# Revit family: QF_Friginox_MX 1 LA TS7-AC
name_source: partatom
category: Specialty Equipment
units: mm (PartAtom-declared; Revit-internal decimal feet)

## family parameters
Always vertical = Yes
Cut with Voids When Loaded = No
Part Type = Normal
Room Calculation Point = No
Round Connector Dimension = Use Diameter
Shared = No
Work Plane-Based = No

## types (2) — shared parameters
Accessory = No
CE Approved = Yes
Chilled Water Return Size = 0 mm
Chilled Water Supply Flow = 0.0 L/s
Chilled Water Supply Size = 0 mm
Condensate Return Connection Height = 105 mm  [stored 0.344488 ft]
Condensate Return Size = 32 mm
Conn Plug = Only cable
Cycle = 50 Hz
D15 = 15 mm  [stored 0.0492126 ft]
Depth Actual = 1091 mm
Description = Blast Chiller, Roll-in 1 trolley GN1/1, 80kg, 110min
Direct Waste Size = 20 mm
Direct Waste_Note = Direct Waste
Door_Depth = 131 mm  [stored 0.42979 ft]
Door_W = 650 mm  [stored 2.13255 ft]
Elec Connection Height = 2030 mm  [stored 6.6601 ft]
Electric power = 5700 W
FL Amps = 0 A
Foodservice Equipment Identifier = Yes
Groupe frigorifique = Logé
Height Actual = 2420 mm  [stored 7.93963 ft]
Identify Quantity as Lot = No
Item Number = FX39272636
Keynote = 0
Length Actual = 1080 mm  [stored 3.54331 ft]
Main switch integrated = No
Manufacturer = FRIGINOX
Mat_Case = QF_Stainless-Brushed
Mat_Clearance = QF_Clearance
Mat_Legs = QF_Stainless-Brushed
Model = MX 1 LA TS7
Number of Poles = 3
Phase = 3
Potential Equalisation = Yes
Refrigerant Compressor Remote = No
Refrigerant Volume = 0.0 L/s
Refrigeration Defrost Drain = Yes
Refrigeration Liquid Line Size = 10 mm
Refrigeration Suction Line Size = 28 mm
URL Cutsheet = FTEC_MX1LATS7_MX1LSTS7_MX1LSXTS7_SXP1LcATS7_SXP1LcSTS7_FR_0922.pdf
URL Manufacturer = http://www.friginox.com
Volt Free Conn = No
Volts = 400 V
Weight = 260.00 kg
zero-valued in all types: Chilled Water Return Connection Height, Chilled Water Supply Connection Height, Cost, Default Elevation, Direct Waste Connection Height, Refrigerant Mass

## per-type parameters (varying)
| type | LH | RH |
| MX 1 LA TS7_RH | No | Yes |
| MX 1 LA TS7_LH | Yes | No |

note: [stored X ft] marks values corroborated as IEEE doubles in the binary element streams (Revit-internal decimal feet)

## geometry (parser evidence)
native form markers: Sweep x16
no freeform markers — native parametric forms only
